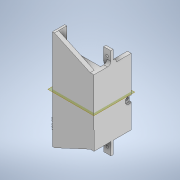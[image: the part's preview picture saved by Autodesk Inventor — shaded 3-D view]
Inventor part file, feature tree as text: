
AUTODESK INVENTOR PART (.ipt)
format: ipt  version: 2020 (Build 240168000, 168)  size: 261,120 bytes
history: native  units: mm
features: sketch x11, extrude x7, other x5, plane x5, mirror x4, hole x4, fillet x2, pattern_linear x1
ambient origin geometry x8: Origin, YZ Plane, XZ Plane, XY Plane, X Axis, Y Axis, Z Axis, Center Point
bodies: Solid1 (feature_tree)
feature tree (39):
  other  "Annotations"
  plane  "Work Plane1"
  extrude  "Extrusion1"  Depth=10.0mm TaperAngle=0.0deg
  plane  "Work Plane2"
  extrude  "Extrusion2"  Depth=30.0mm TaperAngle=0.0deg
  extrude  "Extrusion3"  Depth=86.254mm TaperAngle=0.0deg
  extrude  "Extrusion5"  Depth=8.0mm
  extrude  "Extrusion6"  Depth=240.0mm
  plane  "Work Plane3"
  mirror  "Mirror1"
  plane  "Work Plane4"
  sketch  "Sketch10"  dims[d39=20.0mm d40=240.0mm]
  extrude  "Extrusion7"  Depth=160.0mm
  pattern_linear  "Rectangular Pattern1"  Count1=4  [1 undecoded]
  hole  "Hole2"  [1 undecoded]
  mirror  "Mirror2"
  hole  "Hole3"  [1 undecoded]
  mirror  "Mirror3"
  extrude  "Extrusion9"  Depth=8.0mm
  mirror  "Mirror4"
  fillet  "Fillet1"  Radius=8.0mm
  fillet  "Fillet2"  Radius=100.0mm
  hole  "Hole1"  [1 undecoded]
  sketch  "Sketch1"  dims[d0=5.0mm d1=0.0mm d2=10.0mm d3=0.0mm]
  sketch  "Sketch3"  dims[d4=80.0mm d5=0.0mm d10=30.0mm d11=0.0mm]
  sketch  "Sketch4"  dims[d13=10.0mm d14=0.0mm d15=86.254mm d16=0.0mm]
  sketch  "Sketch6"  dims[d17=60.0mm d19=30.4mm]
  sketch  "Sketch7"  dims[d28=10.0mm d29=6.0mm d30=4.0mm d31=2.0mm d32=90.0deg d33=8.0mm d34=20.594885mm d38=15.0mm]
  sketch  "Sketch11"  dims[d41=20.0mm d42=160.0mm d43=40.0mm]
  sketch  "Sketch14"  dims[d45=6.0mm d46=6.0mm d47=4.0mm d48=2.0mm d49=90.0deg d50=8.0mm d51=20.594885mm d52=15.0mm]
  sketch  "Sketch15"  dims[d53=9.0mm d54=180.0mm d55=0.0mm]
  plane  "Work Plane5"
  sketch  "Sketch16"  dims[d56=240.0mm d57=8.0mm d58=8.0mm]
  sketch  "Sketch17"  dims[d59=6.6mm d60=6.0mm d61=18.0mm d62=4.8mm d63=90.0deg d64=8.0mm d65=0.0mm d44=100.0mm d21=1.0mm d22=1.0mm d23=1.0mm d24=0.15mm d25=8.0mm d26=0.375mm d27=14.3117mm]
  hole  "Hole4"  [1 undecoded]
  other  "Linear Dimension 1"
  parser-record x1  (decoder bookkeeping rows leaked as tree rows — omitted from the tree; the rows remain in map.json)
  other  "robot morango.iam"
  other  "guia:4"
note: 5 required parameter values undecoded (feature->parameter linkage not recoverable at this tier; creation-order binding heuristic only, values carry confidence <= 0.55)
note: 1 file-system path scrubbed to <path> (originals preserved in map.json)
